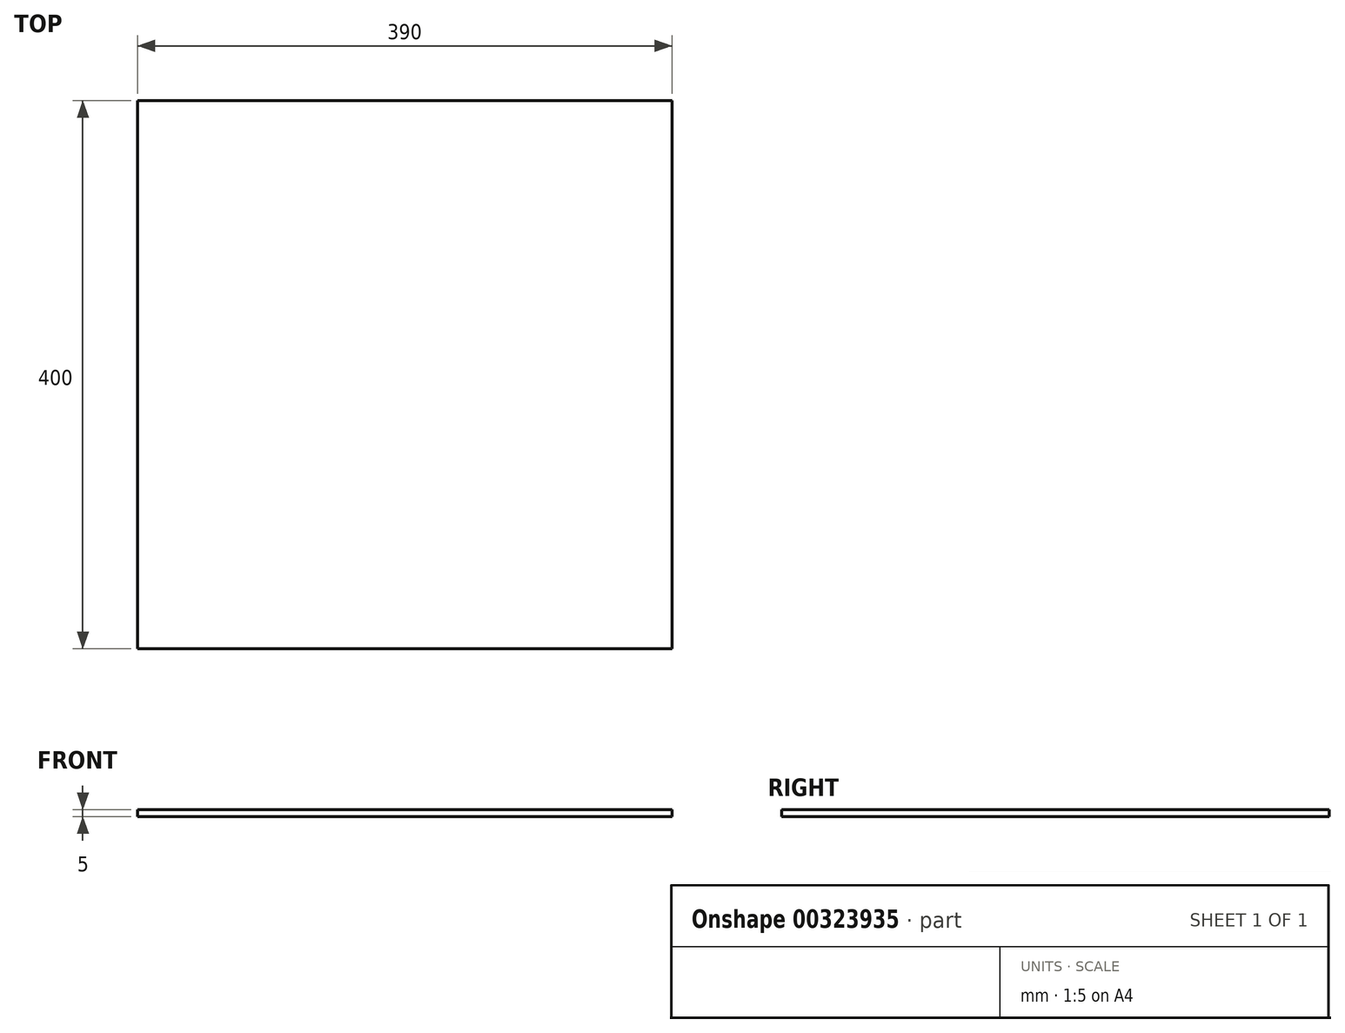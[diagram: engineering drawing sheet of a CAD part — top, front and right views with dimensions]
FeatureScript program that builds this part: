
annotation { "Feature Type Name" : "Feature", "Feature Type Description" : "" }
export const myFeature = defineFeature(function(context is Context, id is Id, definition is map)
    precondition{}
    {
        {
            var Q0;
            Q0=qCreatedBy(makeId("Top.planeOp"),FACE);
            var sketch = newSketch(context, id + "F0", { "sketchPlane" : qUnion([Q0])});
            skLineSegment(sketch, "E0.bottom", {"start": v(-200, 200) * mm, "end": v(200, 200) * mm});
            skLineSegment(sketch, "E0.top", {"start": v(-200, -200) * mm, "end": v(200, -200) * mm});
            skLineSegment(sketch, "E0.right", {"start": v(200, 200) * mm, "end": v(200, -200) * mm});
            skLineSegment(sketch, "E1", {"start": v(-200, 200) * mm, "end": v(-200, -200) * mm});
            skLineSegment(sketch, "E2", {"start": v(-200, 200) * mm, "end": v(190, 200) * mm});
            skLineSegment(sketch, "E3", {"start": v(190, 200) * mm, "end": v(190, -200) * mm});
            skSolve(sketch);
        }
        {
            var Q0;
            {var subQ0=sQuery(id+"F0.wireOp",EDGE,"E1");Q0=makeQuery(id+"F0.imprint","IMPRINT",FACE,{"disambiguationData":[TD([[makeQuery(id+"F0.imprint","IMPRINT",EDGE,{"derivedFrom":subQ0}),1.0]])]});}
            extrude(context, id + "F1", {"entities" : qUnion([Q0]), "depth" : 5 * mm});
        }
    });
